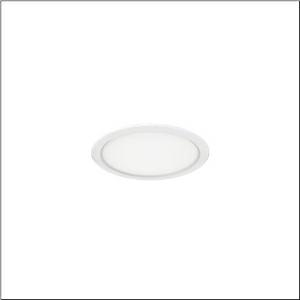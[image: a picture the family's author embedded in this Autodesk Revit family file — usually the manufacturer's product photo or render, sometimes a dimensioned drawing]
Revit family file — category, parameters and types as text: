
# Revit family: lunis_41_eco_51ds107d33a
name_source: partatom
category: Lighting Fixtures
units: mm (PartAtom-declared; Revit-internal decimal feet)

## family parameters
Cut with Voids When Loaded = No
Host = Face
Light Source = No
Part Type = Normal
Room Calculation Point = No
Round Connector Dimension = Use Diameter
Shared = No

## types (1)
- Lunis 41 ECO (1 x LED, 1400 lm, 14 W, 3000K)
    Apparent Load = 14 VA
    CIE Flux Codes = 47 80 97 100 100
    Color Rendering = 80
    Color Temperature = 3000K
    Default Elevation = 1800 mm
    Description = Lunis 41,  ECO, downlight, light emission: direct distribution, LED rated luminous flux: 1.400lm, light colour: 830, control gear: ECG, mains connection: 230V, AC, 50/60Hz, housing, round, of aluminium, coated, traffic white (RAL 9016), diameter: 166mm, recess depth: 54mm, protection rating (complete): IP20, insulation class (complete): insulation class II (safety insulation), certification: CE, permissible ambient temperature for indoor applications: -20..+40°C, packaging unit: 1 piece
    Height = 0 mm  [stored 0 ft]
    Lamp = 1 x LED
    Lamp Light Flux = 1400 lm
    Lamp Power = 14 W
    Lamp count = 1
    Length = 165 mm
    Luminous efficacy = 100 lm/W
    Manufacturer = Siteco
    ModVariant = No
    Model = 51DS107D33A
    Mounting Place = Ceiling
    Mounting Type = Recessed
    Number of Poles = 1
    OnlyDefault = Yes
    Power Factor = 1
    Product Name = Lunis 41 ECO
    Product group = downlight | ceiling recessed
    ProductGroupID = 402
    Protection Class = Protection class II
    Protection Degree = IP 20
    RLX_Detail_Level = 1
    RlxData = <blob elided: 25801 chars, md5=51d3890b>
    Socket = socket
    Standby Power = 0 W
    System Light Flux = 1400 lm
    System Power = 14 W
    Type Comments = Product without accessories
    Type Image = l_1007041.jpg
    URL = http://relux.com
    VarID = ---
    Voltage = 0 V
    Weight = 0.00 kg
    Width = 0 mm  [stored 0 ft]

note: [stored X ft] marks values corroborated as IEEE doubles in the binary element streams (Revit-internal decimal feet)

## geometry (parser evidence)
native form markers: Blend x4, Sweep x11
no freeform markers — native parametric forms only
